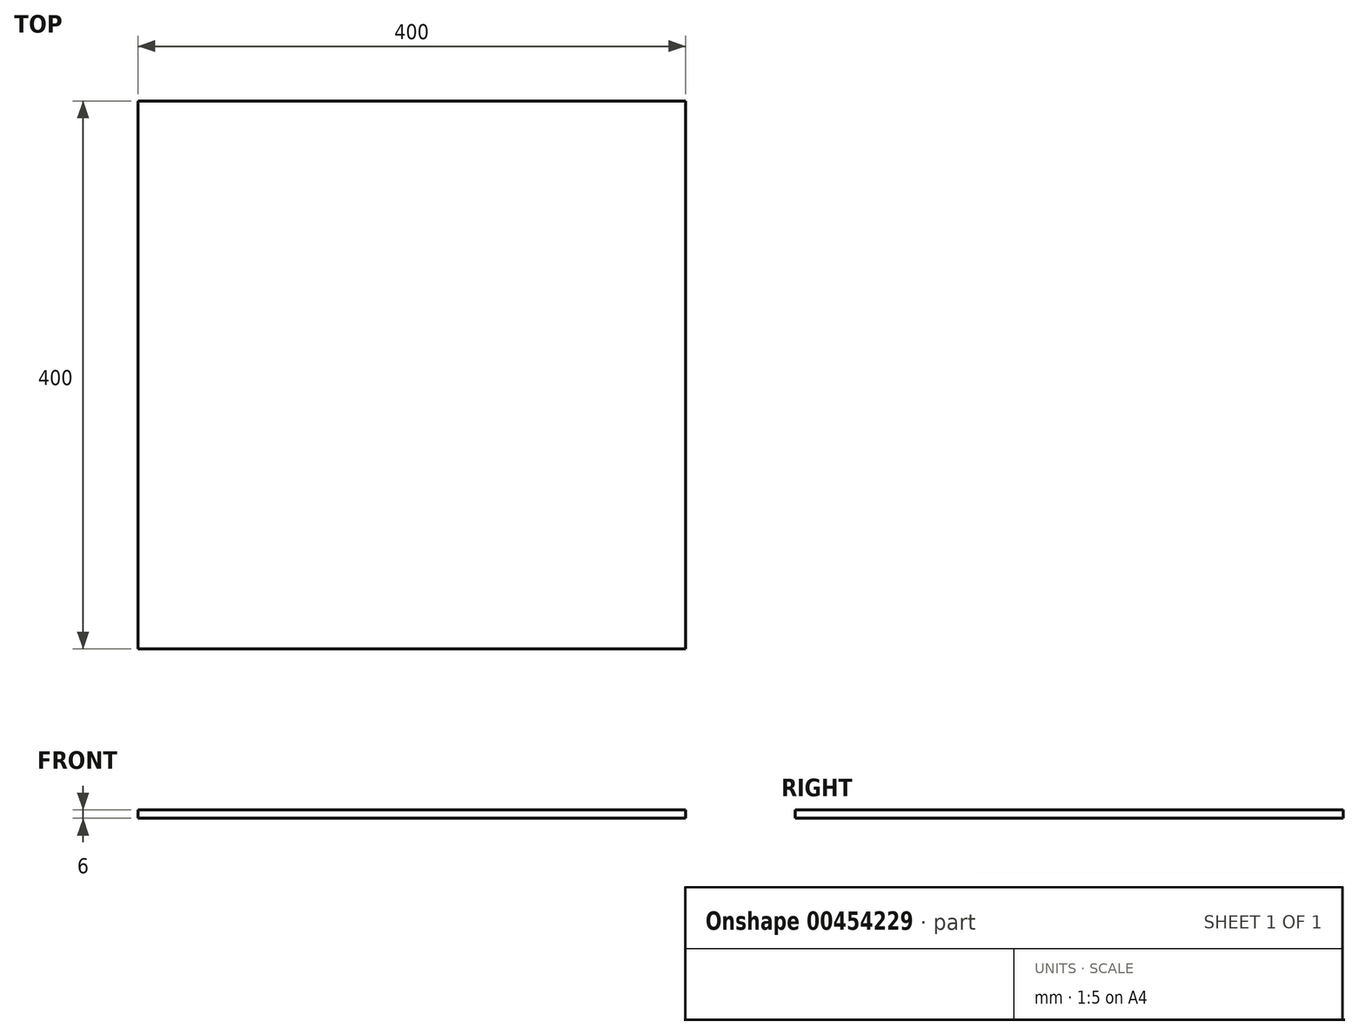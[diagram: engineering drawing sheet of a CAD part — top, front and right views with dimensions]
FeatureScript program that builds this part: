
annotation { "Feature Type Name" : "Feature", "Feature Type Description" : "" }
export const myFeature = defineFeature(function(context is Context, id is Id, definition is map)
    precondition{}
    {
        {
            var Q0;
            Q0=qCreatedBy(makeId("Top.planeOp"),FACE);
            var sketch = newSketch(context, id + "F0", { "sketchPlane" : qUnion([Q0])});
            skLineSegment(sketch, "E0.bottom", {"start": v(200, -200) * mm, "end": v(-200, -200) * mm});
            skLineSegment(sketch, "E0.top", {"start": v(200, 200) * mm, "end": v(-200, 200) * mm});
            skLineSegment(sketch, "E0.left", {"start": v(200, -200) * mm, "end": v(200, 200) * mm});
            skLineSegment(sketch, "E0.right", {"start": v(-200, -200) * mm, "end": v(-200, 200) * mm});
            skPoint(sketch, "E0.middle", {"position": v(0, 0) * mm});
            skSolve(sketch);
        }
        {
            var Q0;
            Q0=makeQuery(id+"F0.imprint","IMPRINT",FACE,{"disambiguationData":[TD([[makeQuery(id+"F0.imprint","IMPRINT",EDGE,{"derivedFrom":sQuery(id+"F0.wireOp",EDGE,"E0.bottom")}),-1.0]])]});
            extrude(context, id + "F1", {"entities" : qUnion([Q0]), "depth" : 6 * mm});
        }
    });
